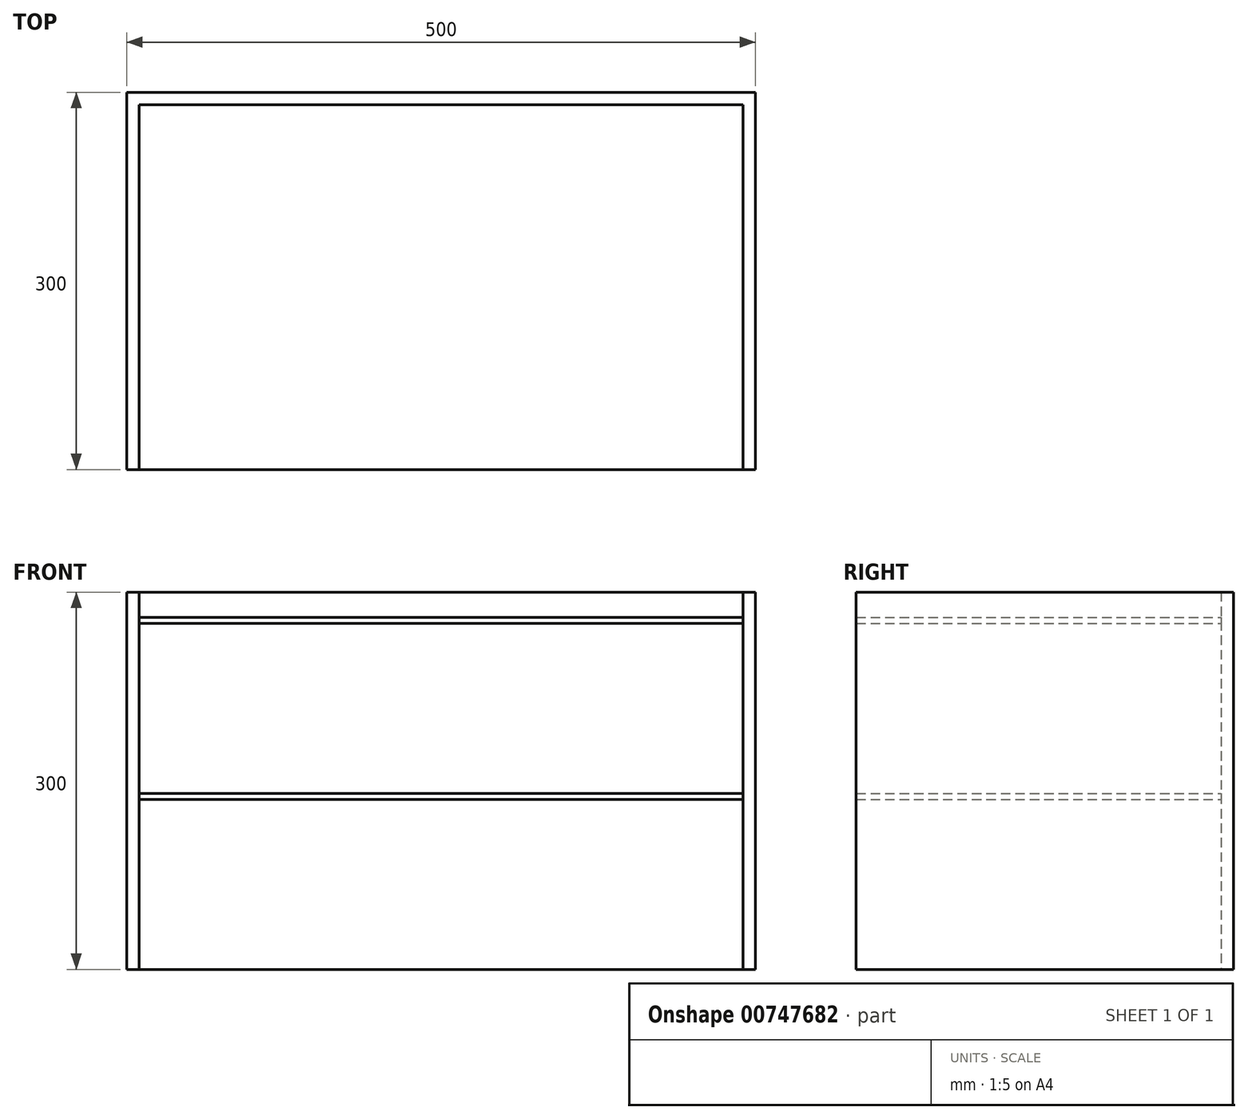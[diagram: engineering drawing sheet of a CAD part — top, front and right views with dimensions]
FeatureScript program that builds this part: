
annotation { "Feature Type Name" : "Feature", "Feature Type Description" : "" }
export const myFeature = defineFeature(function(context is Context, id is Id, definition is map)
    precondition{}
    {
        {
            var Q0;
            Q0=qCreatedBy(makeId("Top.planeOp"),FACE);
            var sketch = newSketch(context, id + "F0", { "sketchPlane" : qUnion([Q0])});
            skLineSegment(sketch, "E0.top", {"start": v(-240.08, 300) * mm, "end": v(259.92, 300) * mm});
            skLineSegment(sketch, "E0.left", {"start": v(-240.08, 0) * mm, "end": v(-240.08, 300) * mm});
            skLineSegment(sketch, "E0.right", {"start": v(259.92, 0) * mm, "end": v(259.92, 300) * mm});
            skLineSegment(sketch, "E1.0", {"start": v(-230.08, 290) * mm, "end": v(249.92, 290) * mm});
            skLineSegment(sketch, "E1.1", {"start": v(-230.08, 0) * mm, "end": v(-230.08, 290) * mm});
            skLineSegment(sketch, "E1.3", {"start": v(249.92, 0) * mm, "end": v(249.92, 290) * mm});
            skLineSegment(sketch, "E2", {"start": v(-240.08, 0) * mm, "end": v(-230.08, 0) * mm});
            skLineSegment(sketch, "E3", {"start": v(249.92, 0) * mm, "end": v(259.92, 0) * mm});
            skSolve(sketch);
        }
        {
            var Q0;
            Q0 = qSketchRegion(id + "F0", true);
            extrude(context, id + "F1", {"entities" : qUnion([Q0]), "depth" : 300 * mm, "offsetDistance" : 25 * mm});
        }
        {
            var Q0;
            Q0=qCreatedBy(makeId("Top.planeOp"),FACE);
            cPlane(context, id + "F2", {"entities" : qUnion([Q0]), "cplaneType" : CPlaneType.OFFSET, "offset" : 135 * mm, "width" : 150 * mm, "height" : 150 * mm});
        }
        {
            var Q0;
            Q0=qCreatedBy(id+"F2.planeOp",FACE);
            var sketch = newSketch(context, id + "F3", { "sketchPlane" : qUnion([Q0])});
            skLineSegment(sketch, "E4.bottom", {"start": v(-230.08, 0) * mm, "end": v(249.92, 0) * mm});
            skLineSegment(sketch, "E4.top", {"start": v(-230.08, 290) * mm, "end": v(249.92, 290) * mm});
            skLineSegment(sketch, "E4.left", {"start": v(-230.08, 0) * mm, "end": v(-230.08, 290) * mm});
            skLineSegment(sketch, "E4.right", {"start": v(249.92, 0) * mm, "end": v(249.92, 290) * mm});
            skSolve(sketch);
        }
        {
            var Q0;
            Q0 = qSketchRegion(id + "F3", true);
            extrude(context, id + "F4", {"entities" : qUnion([Q0]), "depth" : 5 * mm, "offsetDistance" : 25 * mm});
        }
        {
            var Q0;
            Q0=makeQuery(id+"F4.opExtrude","CAP_FACE",FACE,{"disambiguationData":[OSD([sQuery(id+"F3.wireOp",EDGE,"E4.bottom"),sQuery(id+"F3.wireOp",EDGE,"E4.top"),sQuery(id+"F3.wireOp",EDGE,"E4.left"),sQuery(id+"F3.wireOp",EDGE,"E4.right")])],"isStart":false});
            cPlane(context, id + "F5", {"entities" : qUnion([Q0]), "cplaneType" : CPlaneType.OFFSET, "offset" : 135 * mm, "width" : 150 * mm, "height" : 150 * mm});
        }
        {
            var Q0;
            Q0=qCreatedBy(id+"F5.planeOp",FACE);
            var sketch = newSketch(context, id + "F6", { "sketchPlane" : qUnion([Q0])});
            skLineSegment(sketch, "E5.bottom", {"start": v(-230.08, 0) * mm, "end": v(249.92, 0) * mm});
            skLineSegment(sketch, "E5.top", {"start": v(-230.08, 290) * mm, "end": v(249.92, 290) * mm});
            skLineSegment(sketch, "E5.left", {"start": v(-230.08, 0) * mm, "end": v(-230.08, 290) * mm});
            skLineSegment(sketch, "E5.right", {"start": v(249.92, 0) * mm, "end": v(249.92, 290) * mm});
            skSolve(sketch);
        }
        {
            var Q0;
            Q0 = qSketchRegion(id + "F6", true);
            extrude(context, id + "F7", {"entities" : qUnion([Q0]), "depth" : 5 * mm, "offsetDistance" : 25 * mm});
        }
    });
